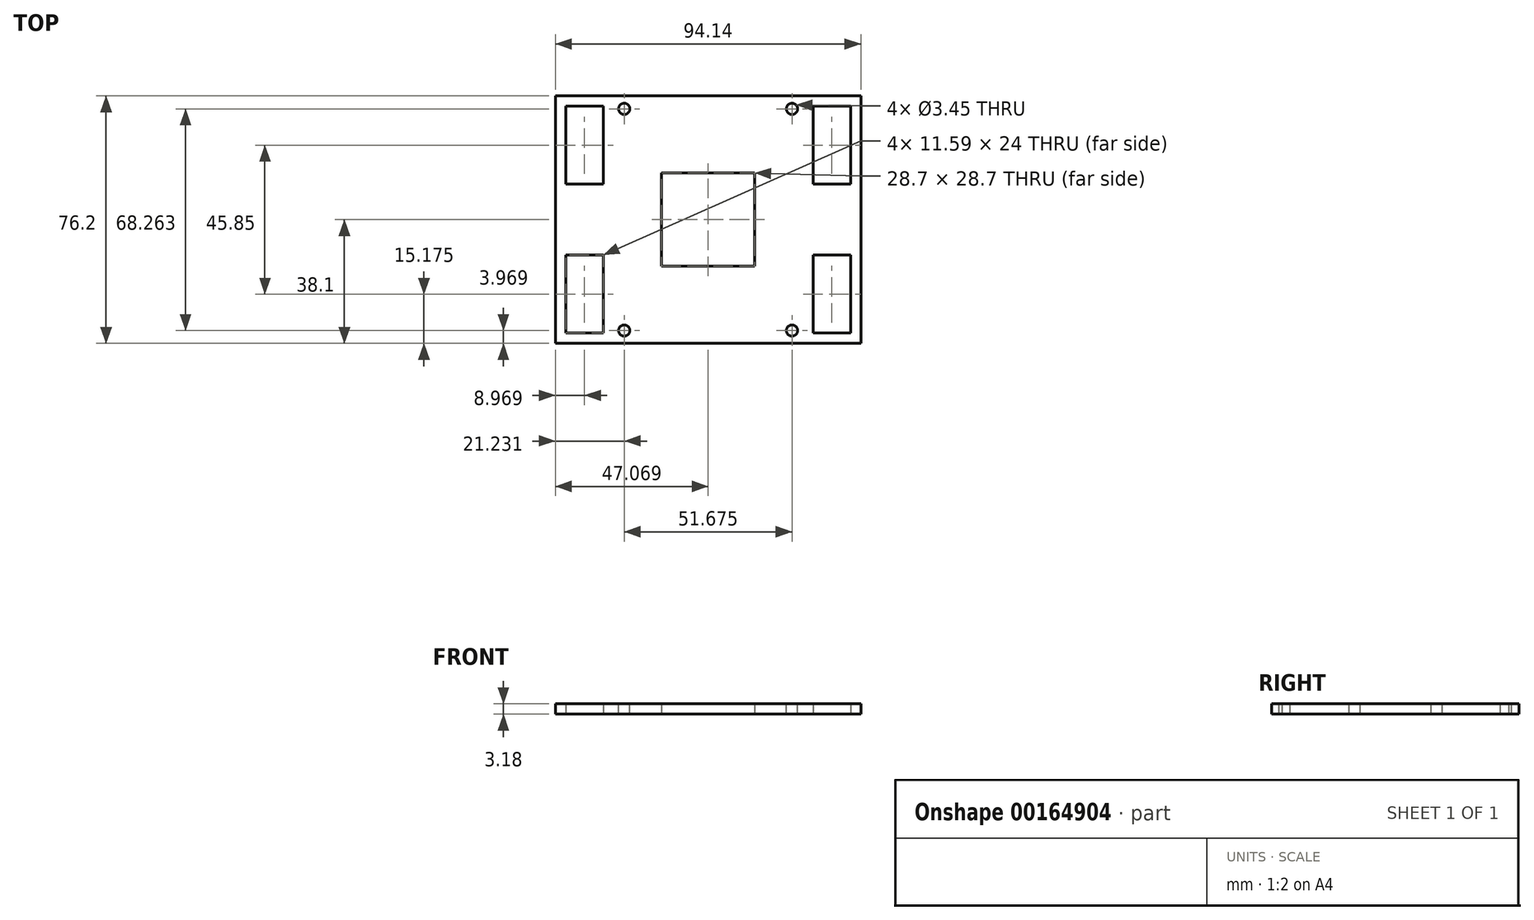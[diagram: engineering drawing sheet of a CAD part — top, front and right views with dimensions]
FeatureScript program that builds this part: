
annotation { "Feature Type Name" : "Feature", "Feature Type Description" : "" }
export const myFeature = defineFeature(function(context is Context, id is Id, definition is map)
    precondition{}
    {
        {
            var Q0;
            Q0=qCreatedBy(makeId("Top.planeOp"),FACE);
            var sketch = newSketch(context, id + "F0", { "sketchPlane" : qUnion([Q0])});
            skLineSegment(sketch, "E0.bottom", {"start": v(0, 0) * mm, "end": v(94.14, 0) * mm});
            skLineSegment(sketch, "E0.top", {"start": v(0, -76.2) * mm, "end": v(94.14, -76.2) * mm});
            skLineSegment(sketch, "E0.left", {"start": v(0, 0) * mm, "end": v(0, -76.2) * mm});
            skLineSegment(sketch, "E0.right", {"start": v(94.14, 0) * mm, "end": v(94.14, -76.2) * mm});
            skLineSegment(sketch, "E1", {"start": v(47.07, 0) * mm, "end": v(47.07, -76.2) * mm, "construction": true});
            skLineSegment(sketch, "E2.bottom", {"start": v(85.17, -15.18) * mm, "end": v(8.97, -15.18) * mm, "construction": true});
            skLineSegment(sketch, "E2.top", {"start": v(85.17, -61.03) * mm, "end": v(8.97, -61.03) * mm, "construction": true});
            skLineSegment(sketch, "E2.left", {"start": v(85.17, -15.18) * mm, "end": v(85.17, -61.03) * mm, "construction": true});
            skLineSegment(sketch, "E2.right", {"start": v(8.97, -15.18) * mm, "end": v(8.97, -61.03) * mm, "construction": true});
            skPoint(sketch, "E2.middle", {"position": v(47.07, -38.1) * mm});
            skLineSegment(sketch, "E3.bottom", {"start": v(90.96, -3.18) * mm, "end": v(79.38, -3.18) * mm});
            skLineSegment(sketch, "E3.top", {"start": v(90.96, -27.18) * mm, "end": v(79.38, -27.18) * mm});
            skLineSegment(sketch, "E3.left", {"start": v(90.96, -3.18) * mm, "end": v(90.96, -27.17) * mm});
            skLineSegment(sketch, "E3.right", {"start": v(79.38, -3.18) * mm, "end": v(79.38, -27.18) * mm});
            skPoint(sketch, "E3.middle", {"position": v(85.17, -15.18) * mm});
            skLineSegment(sketch, "E4.bottom", {"start": v(90.96, -73.03) * mm, "end": v(79.37, -73.03) * mm});
            skLineSegment(sketch, "E4.top", {"start": v(90.96, -49.03) * mm, "end": v(79.37, -49.03) * mm});
            skLineSegment(sketch, "E4.left", {"start": v(90.96, -73.03) * mm, "end": v(90.96, -49.03) * mm});
            skLineSegment(sketch, "E4.right", {"start": v(79.37, -73.03) * mm, "end": v(79.37, -49.03) * mm});
            skPoint(sketch, "E4.middle", {"position": v(85.17, -61.03) * mm});
            skLineSegment(sketch, "E5.bottom", {"start": v(3.17, -73.03) * mm, "end": v(14.76, -73.03) * mm});
            skLineSegment(sketch, "E5.top", {"start": v(3.17, -49.03) * mm, "end": v(14.76, -49.03) * mm});
            skLineSegment(sketch, "E5.left", {"start": v(3.17, -73.03) * mm, "end": v(3.17, -49.03) * mm});
            skLineSegment(sketch, "E5.right", {"start": v(14.76, -73.03) * mm, "end": v(14.76, -49.03) * mm});
            skPoint(sketch, "E5.middle", {"position": v(8.97, -61.03) * mm});
            skLineSegment(sketch, "E6.bottom", {"start": v(3.17, -27.17) * mm, "end": v(14.76, -27.17) * mm});
            skLineSegment(sketch, "E6.top", {"start": v(3.17, -3.18) * mm, "end": v(14.76, -3.18) * mm});
            skLineSegment(sketch, "E6.left", {"start": v(3.17, -27.17) * mm, "end": v(3.17, -3.18) * mm});
            skLineSegment(sketch, "E6.right", {"start": v(14.76, -27.17) * mm, "end": v(14.76, -3.18) * mm});
            skPoint(sketch, "E6.middle", {"position": v(8.97, -15.18) * mm});
            skLineSegment(sketch, "E7.bottom", {"start": v(61.42, -23.75) * mm, "end": v(32.72, -23.75) * mm});
            skLineSegment(sketch, "E7.top", {"start": v(61.42, -52.45) * mm, "end": v(32.72, -52.45) * mm});
            skLineSegment(sketch, "E7.left", {"start": v(61.42, -23.75) * mm, "end": v(61.42, -52.45) * mm});
            skLineSegment(sketch, "E7.right", {"start": v(32.72, -23.75) * mm, "end": v(32.72, -52.45) * mm});
            skSolve(sketch);
        }
        {
            var Q0;
            Q0=qSketchRegion(id+"F0",true);
            extrude(context, id + "F1", {"entities" : qUnion([Q0]), "depth" : 3.17 * mm});
        }
        {
            var Q0;
            Q0=makeQuery(id+"F1.opExtrude","CAP_FACE",FACE,{"disambiguationData":[OSD([sQuery(id+"F0.wireOp",EDGE,"E0.bottom"),sQuery(id+"F0.wireOp",EDGE,"E0.top"),sQuery(id+"F0.wireOp",EDGE,"E0.left"),sQuery(id+"F0.wireOp",EDGE,"E0.right"),sQuery(id+"F0.wireOp",EDGE,"E3.bottom"),sQuery(id+"F0.wireOp",EDGE,"E3.top"),sQuery(id+"F0.wireOp",EDGE,"E3.left"),sQuery(id+"F0.wireOp",EDGE,"E3.right"),sQuery(id+"F0.wireOp",EDGE,"E4.bottom"),sQuery(id+"F0.wireOp",EDGE,"E4.top"),sQuery(id+"F0.wireOp",EDGE,"E4.left"),sQuery(id+"F0.wireOp",EDGE,"E4.right"),sQuery(id+"F0.wireOp",EDGE,"E5.bottom"),sQuery(id+"F0.wireOp",EDGE,"E5.top"),sQuery(id+"F0.wireOp",EDGE,"E5.left"),sQuery(id+"F0.wireOp",EDGE,"E5.right"),sQuery(id+"F0.wireOp",EDGE,"E6.bottom"),sQuery(id+"F0.wireOp",EDGE,"E6.top"),sQuery(id+"F0.wireOp",EDGE,"E6.left"),sQuery(id+"F0.wireOp",EDGE,"E6.right"),sQuery(id+"F0.wireOp",EDGE,"JYg2saEG-vLPU-2o7O-Pn54-yeExWXw8yuXa"),sQuery(id+"F0.wireOp",EDGE,"4E2fAsVk-0vaP-PcjW-vrmz-fDQwhqaWbgNb"),sQuery(id+"F0.wireOp",EDGE,"7VMwEGr7-JVzO-nlXg-rXEM-Mibjjc7mmKUu")])],"isStart":false});
            var sketch = newSketch(context, id + "F2", { "sketchPlane" : qUnion([Q0])});
            skLineSegment(sketch, "E8", {"start": v(8.97, -73.03) * mm, "end": v(8.97, -72.23) * mm, "construction": true});
            skLineSegment(sketch, "E9", {"start": v(8.97, -72.23) * mm, "end": v(21.23, -72.23) * mm, "construction": true});
            skLineSegment(sketch, "E10.bottom", {"start": v(21.23, -72.23) * mm, "end": v(72.9, -72.23) * mm, "construction": true});
            skLineSegment(sketch, "E10.top", {"start": v(21.23, -3.97) * mm, "end": v(72.9, -3.97) * mm, "construction": true});
            skLineSegment(sketch, "E10.left", {"start": v(21.23, -72.23) * mm, "end": v(21.23, -3.97) * mm, "construction": true});
            skLineSegment(sketch, "E10.right", {"start": v(72.9, -72.23) * mm, "end": v(72.9, -3.97) * mm, "construction": true});
            skPoint(sketch, "E10.middle", {"position": v(47.07, -38.1) * mm});
            skCircle(sketch, "E11", {"center": v(21.23, -3.97) * mm, "radius": 1.73 * mm});
            skCircle(sketch, "E12", {"center": v(72.9, -3.97) * mm, "radius": 1.73 * mm});
            skCircle(sketch, "E13", {"center": v(72.9, -72.23) * mm, "radius": 1.73 * mm});
            skCircle(sketch, "E14", {"center": v(21.23, -72.23) * mm, "radius": 1.73 * mm});
            skLineSegment(sketch, "E15", {"start": v(47.07, -23.75) * mm, "end": v(47.07, -52.45) * mm, "construction": true});
            skSolve(sketch);
        }
        {
            var Q0;
            Q0=qSketchRegion(id+"F2",true);
            var Q1;
            Q1=makeQuery(id+"F1.opExtrude","CAP_FACE",FACE,{"disambiguationData":[OSD([sQuery(id+"F0.wireOp",EDGE,"E0.bottom"),sQuery(id+"F0.wireOp",EDGE,"E0.top"),sQuery(id+"F0.wireOp",EDGE,"E0.left"),sQuery(id+"F0.wireOp",EDGE,"E0.right"),sQuery(id+"F0.wireOp",EDGE,"E3.bottom"),sQuery(id+"F0.wireOp",EDGE,"E3.top"),sQuery(id+"F0.wireOp",EDGE,"E3.left"),sQuery(id+"F0.wireOp",EDGE,"E3.right"),sQuery(id+"F0.wireOp",EDGE,"E4.bottom"),sQuery(id+"F0.wireOp",EDGE,"E4.top"),sQuery(id+"F0.wireOp",EDGE,"E4.left"),sQuery(id+"F0.wireOp",EDGE,"E4.right"),sQuery(id+"F0.wireOp",EDGE,"E5.bottom"),sQuery(id+"F0.wireOp",EDGE,"E5.top"),sQuery(id+"F0.wireOp",EDGE,"E5.left"),sQuery(id+"F0.wireOp",EDGE,"E5.right"),sQuery(id+"F0.wireOp",EDGE,"E6.bottom"),sQuery(id+"F0.wireOp",EDGE,"E6.top"),sQuery(id+"F0.wireOp",EDGE,"E6.left"),sQuery(id+"F0.wireOp",EDGE,"E6.right"),sQuery(id+"F0.wireOp",EDGE,"JYg2saEG-vLPU-2o7O-Pn54-yeExWXw8yuXa"),sQuery(id+"F0.wireOp",EDGE,"4E2fAsVk-0vaP-PcjW-vrmz-fDQwhqaWbgNb"),sQuery(id+"F0.wireOp",EDGE,"7VMwEGr7-JVzO-nlXg-rXEM-Mibjjc7mmKUu")])],"isStart":true});
            extrude(context, id + "F3", {"entities" : qUnion([Q0]), "operationType" : NewBodyOperationType.REMOVE, "endBound" : BoundingType.UP_TO_SURFACE, "oppositeDirection" : true, "endBoundEntityFace" : qUnion([Q1]), "depth" : 25.4 * mm});
        }
    });
